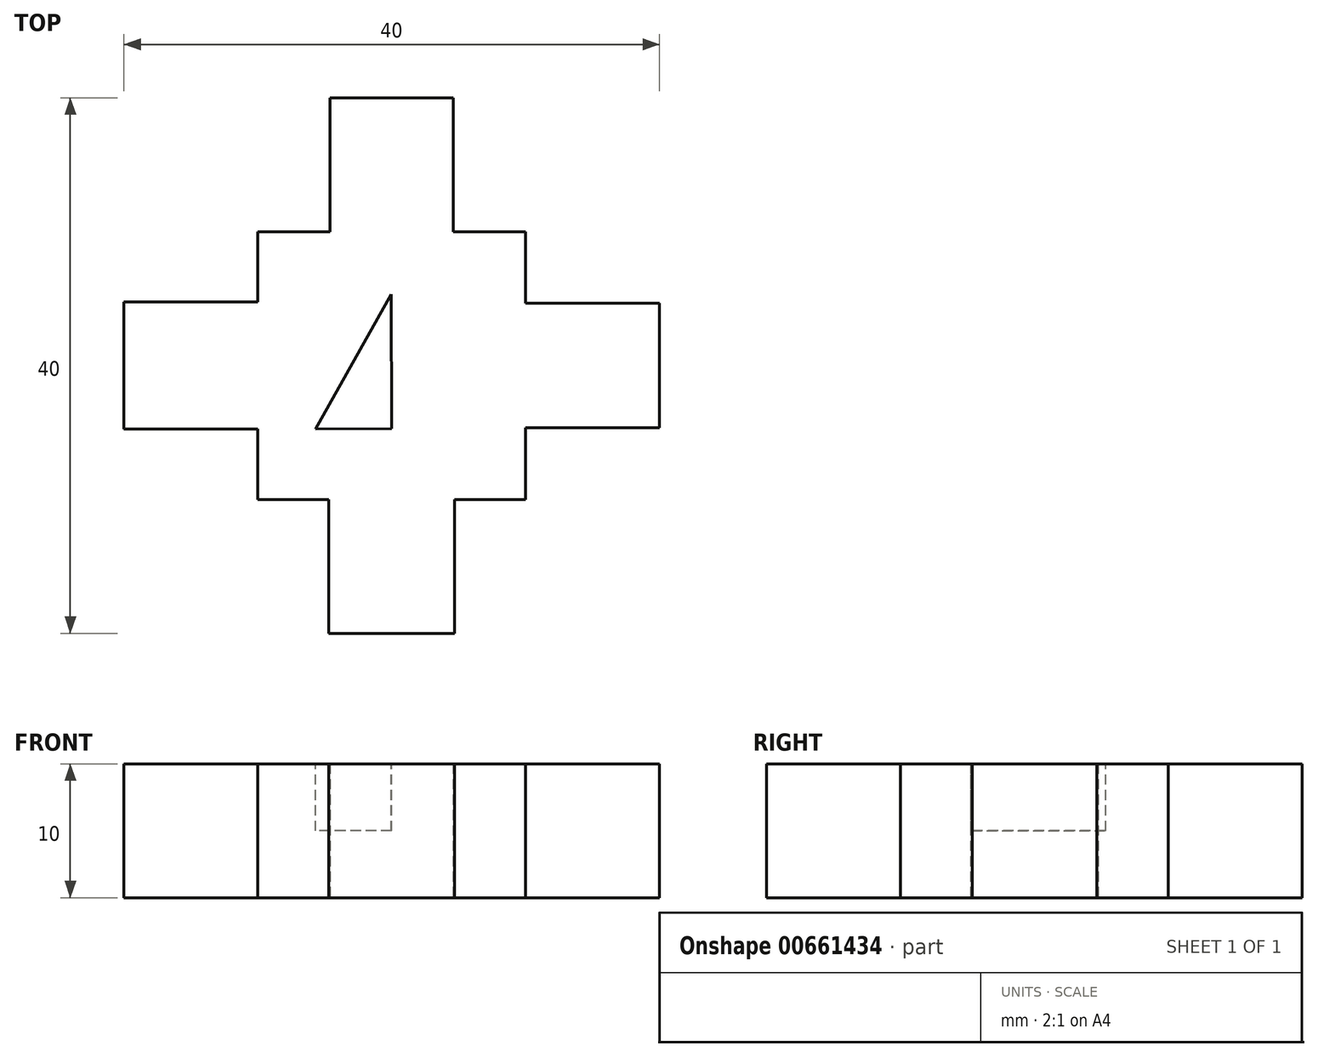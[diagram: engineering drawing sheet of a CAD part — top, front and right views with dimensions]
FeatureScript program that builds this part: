
annotation { "Feature Type Name" : "Feature", "Feature Type Description" : "" }
export const myFeature = defineFeature(function(context is Context, id is Id, definition is map)
    precondition{}
    {
        {
            var Q0;
            Q0=qCreatedBy(makeId("Top.planeOp"),FACE);
            var sketch = newSketch(context, id + "F0", { "sketchPlane" : qUnion([Q0])});
            skLineSegment(sketch, "E0", {"start": v(0, 0) * mm, "end": v(20, 0) * mm});
            skLineSegment(sketch, "E1", {"start": v(20, 0) * mm, "end": v(20, -20) * mm});
            skLineSegment(sketch, "E2", {"start": v(20, -20) * mm, "end": v(0, -20) * mm});
            skLineSegment(sketch, "E3", {"start": v(0, -20) * mm, "end": v(0, 0) * mm});
            skLineSegment(sketch, "E4", {"start": v(0, -10) * mm, "end": v(-10, -10) * mm});
            skLineSegment(sketch, "E5", {"start": v(10, 0) * mm, "end": v(10, 10) * mm});
            skLineSegment(sketch, "E6", {"start": v(20, -10) * mm, "end": v(30, -10) * mm});
            skLineSegment(sketch, "E7", {"start": v(10, -20) * mm, "end": v(10, -30) * mm});
            skLineSegment(sketch, "E8", {"start": v(10, 10) * mm, "end": v(5.4, 10) * mm});
            skLineSegment(sketch, "E9", {"start": v(10, 10) * mm, "end": v(14.6, 10) * mm});
            skLineSegment(sketch, "E10", {"start": v(14.6, 10) * mm, "end": v(14.6, 0) * mm});
            skLineSegment(sketch, "E11", {"start": v(5.4, 10) * mm, "end": v(5.4, 0) * mm});
            skLineSegment(sketch, "E12", {"start": v(30, -10) * mm, "end": v(30, -5.35) * mm});
            skLineSegment(sketch, "E13", {"start": v(30, -10) * mm, "end": v(30, -14.65) * mm});
            skLineSegment(sketch, "E14", {"start": v(30, -14.65) * mm, "end": v(20, -14.65) * mm});
            skLineSegment(sketch, "E15", {"start": v(30, -5.35) * mm, "end": v(20, -5.35) * mm});
            skLineSegment(sketch, "E16", {"start": v(10, -30) * mm, "end": v(14.7, -30) * mm});
            skLineSegment(sketch, "E17", {"start": v(14.7, -30) * mm, "end": v(14.7, -20) * mm});
            skLineSegment(sketch, "E18", {"start": v(10, -30) * mm, "end": v(5.3, -30) * mm});
            skLineSegment(sketch, "E19", {"start": v(5.3, -30) * mm, "end": v(5.3, -20) * mm});
            skLineSegment(sketch, "E20", {"start": v(-10, -10) * mm, "end": v(-10, -5.25) * mm});
            skLineSegment(sketch, "E21", {"start": v(-10, -5.25) * mm, "end": v(0, -5.25) * mm});
            skLineSegment(sketch, "E22", {"start": v(-10, -10) * mm, "end": v(-10, -14.75) * mm});
            skLineSegment(sketch, "E23", {"start": v(-10, -14.75) * mm, "end": v(0, -14.75) * mm});
            skSolve(sketch);
        }
        {
            var Q0;
            Q0 = qSketchRegion(id + "F0", true);
            extrude(context, id + "F1", {"entities" : qUnion([Q0]), "depth" : 10 * mm, "offsetDistance" : 25 * mm});
        }
        {
            var Q0;
            Q0=makeQuery(id+"F1.opExtrude","CAP_FACE",FACE,{"disambiguationData":[OSD([sQuery(id+"F0.wireOp",EDGE,"E0"),sQuery(id+"F0.wireOp",EDGE,"E1"),sQuery(id+"F0.wireOp",EDGE,"E2"),sQuery(id+"F0.wireOp",EDGE,"E3"),sQuery(id+"F0.wireOp",EDGE,"E8"),sQuery(id+"F0.wireOp",EDGE,"E9"),sQuery(id+"F0.wireOp",EDGE,"E10"),sQuery(id+"F0.wireOp",EDGE,"E11"),sQuery(id+"F0.wireOp",EDGE,"E12"),sQuery(id+"F0.wireOp",EDGE,"E13"),sQuery(id+"F0.wireOp",EDGE,"E14"),sQuery(id+"F0.wireOp",EDGE,"E15"),sQuery(id+"F0.wireOp",EDGE,"E16"),sQuery(id+"F0.wireOp",EDGE,"E17"),sQuery(id+"F0.wireOp",EDGE,"E18"),sQuery(id+"F0.wireOp",EDGE,"E19"),sQuery(id+"F0.wireOp",EDGE,"E20"),sQuery(id+"F0.wireOp",EDGE,"E21"),sQuery(id+"F0.wireOp",EDGE,"E22"),sQuery(id+"F0.wireOp",EDGE,"E23")])],"isStart":false});
            var sketch = newSketch(context, id + "F2", { "sketchPlane" : qUnion([Q0])});
            skLineSegment(sketch, "E24", {"start": v(20, -14.65) * mm, "end": v(0, -14.75) * mm});
            skLineSegment(sketch, "E25", {"start": v(10, -14.7) * mm, "end": v(9.95, -4.67) * mm});
            skLineSegment(sketch, "E26", {"start": v(9.95, -4.67) * mm, "end": v(4.3, -14.73) * mm});
            skSolve(sketch);
        }
        {
            var Q0;
            Q0 = qSketchRegion(id + "F2", true);
            extrude(context, id + "F3", {"entities" : qUnion([Q0]), "operationType" : NewBodyOperationType.REMOVE, "oppositeDirection" : true, "depth" : 5 * mm, "offsetDistance" : 25 * mm});
        }
    });
